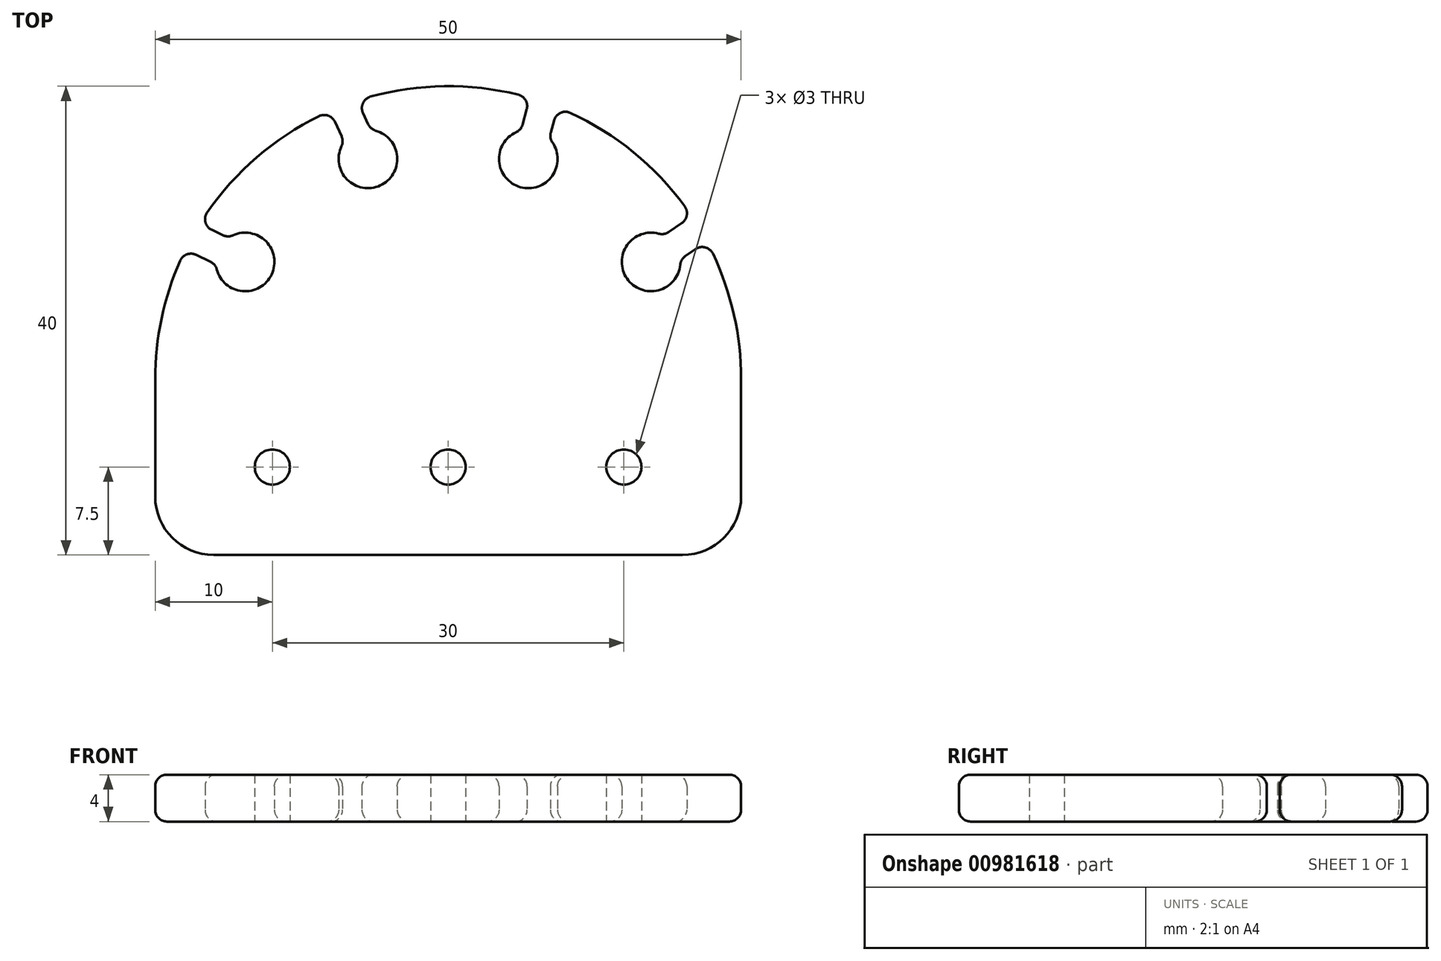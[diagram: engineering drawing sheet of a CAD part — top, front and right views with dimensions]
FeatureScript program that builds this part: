
annotation { "Feature Type Name" : "Feature", "Feature Type Description" : "" }
export const myFeature = defineFeature(function(context is Context, id is Id, definition is map)
    precondition{}
    {
        {
            var Q0;
            Q0=qCreatedBy(makeId("Top.planeOp"),FACE);
            var sketch = newSketch(context, id + "F0", { "sketchPlane" : qUnion([Q0])});
            skCircle(sketch, "E0", {"center": v(-17.32, 25) * mm, "radius": 2.5 * mm});
            skLineSegment(sketch, "E1", {"start": v(-17.32, 25) * mm, "end": v(-21.85, 27.15) * mm, "construction": true});
            skLineSegment(sketch, "E2.0", {"start": v(-14.98, 25.27) * mm, "end": v(-22.2, 28.7) * mm});
            skLineSegment(sketch, "E3.MirrorCS", {"start": v(-16.05, 23.01) * mm, "end": v(-23.28, 26.45) * mm});
            skCircle(sketch, "E4", {"center": v(0, 15) * mm, "radius": 25 * mm});
            skCircle(sketch, "E5.1.0", {"center": v(-6.84, 33.8) * mm, "radius": 2.5 * mm});
            skLineSegment(sketch, "E5.1.1", {"start": v(-7.15, 31.46) * mm, "end": v(-10.47, 38.73) * mm});
            skLineSegment(sketch, "E5.1.2", {"start": v(-4.87, 32.5) * mm, "end": v(-8.2, 39.77) * mm});
            skCircle(sketch, "E5.2.0", {"center": v(6.84, 33.8) * mm, "radius": 2.5 * mm});
            skLineSegment(sketch, "E5.2.1", {"start": v(5.1, 32.2) * mm, "end": v(7.23, 39.91) * mm});
            skLineSegment(sketch, "E5.2.2", {"start": v(7.51, 31.53) * mm, "end": v(9.64, 39.25) * mm});
            skCircle(sketch, "E5.3.0", {"center": v(17.32, 25) * mm, "radius": 2.5 * mm});
            skLineSegment(sketch, "E5.3.1", {"start": v(14.96, 24.9) * mm, "end": v(21.55, 29.43) * mm});
            skLineSegment(sketch, "E5.3.2", {"start": v(16.38, 22.84) * mm, "end": v(22.97, 27.38) * mm});
            skLineSegment(sketch, "E5.anchor1", {"start": v(0, 15) * mm, "end": v(-17.32, 25) * mm, "construction": true});
            skLineSegment(sketch, "E5.anchor2", {"start": v(0, 15) * mm, "end": v(17.32, 25) * mm, "construction": true});
            skLineSegment(sketch, "E6.bottom", {"start": v(-25, 15) * mm, "end": v(25, 15) * mm});
            skLineSegment(sketch, "E6.left", {"start": v(-25, 15) * mm, "end": v(-25, 0) * mm});
            skLineSegment(sketch, "E6.right", {"start": v(25, 15) * mm, "end": v(25, 0) * mm});
            skLineSegment(sketch, "E7", {"start": v(-25, 0) * mm, "end": v(25, 0) * mm});
            skLineSegment(sketch, "E8", {"start": v(-25, 7.5) * mm, "end": v(25, 7.5) * mm, "construction": true});
            skCircle(sketch, "E9", {"center": v(-15, 7.5) * mm, "radius": 1.5 * mm});
            skCircle(sketch, "E10", {"center": v(0, 7.5) * mm, "radius": 1.5 * mm});
            skCircle(sketch, "E11", {"center": v(15, 7.5) * mm, "radius": 1.5 * mm});
            skSolve(sketch);
        }
        {
            var Q0;
            {var subQ20=sQuery(id+"F0.wireOp",EDGE,"E6.bottom");Q0=makeQuery(id+"F0.imprint","IMPRINT",FACE,{"disambiguationData":[TD([[makeQuery(id+"F0.imprint","IMPRINT",EDGE,{"derivedFrom":subQ20}),1.0]])]});}
            var Q1;
            {var subQ4=sQuery(id+"F0.wireOp",EDGE,"E6.bottom");Q1=makeQuery(id+"F0.imprint","IMPRINT",FACE,{"disambiguationData":[TD([[makeQuery(id+"F0.imprint","IMPRINT",EDGE,{"derivedFrom":subQ4}),-1.0]])]});}
            var Q2;
            {var subQ0=sQuery(id+"F0.wireOp",EDGE,"E6.left");Q2=makeQuery(id+"F0.imprint","IMPRINT",FACE,{"disambiguationData":[TD([[makeQuery(id+"F0.imprint","IMPRINT",EDGE,{"derivedFrom":subQ0}),1.0]])]});}
            var Q3;
            {var subQ0=sQuery(id+"F0.wireOp",EDGE,"E6.right");Q3=makeQuery(id+"F0.imprint","IMPRINT",FACE,{"disambiguationData":[TD([[makeQuery(id+"F0.imprint","IMPRINT",EDGE,{"derivedFrom":subQ0}),-1.0]])]});}
            extrude(context, id + "F1", {"entities" : qUnion([Q0, Q1, Q2, Q3]), "depth" : 4 * mm, "offsetDistance" : 25 * mm});
        }
        {
            var Q0;
            Q0=makeQuery(id+"F1.opExtrude","SWEPT_EDGE",EDGE,{"disambiguationData":[OSD([sQuery(id+"F0.wireOp",EDGE,"E6.left"),sQuery(id+"F0.wireOp",EDGE,"E7")])]});
            var Q1;
            Q1=makeQuery(id+"F1.opExtrude","SWEPT_EDGE",EDGE,{"disambiguationData":[OSD([sQuery(id+"F0.wireOp",EDGE,"E6.right"),sQuery(id+"F0.wireOp",EDGE,"E7")])]});
            fillet(context, id + "F2", {"entities" : qUnion([Q0, Q1]), "radius" : 5 * mm, "tangentPropagation" : true, "allowEdgeOverflow" : false});
        }
        {
            var Q0;
            Q0=makeQuery(id+"F1.opExtrude","SWEPT_EDGE",EDGE,{"disambiguationData":[OSD([sQuery(id+"F0.wireOp",EDGE,"E4"),sQuery(id+"F0.wireOp",EDGE,"E5.3.2")])]});
            var Q1;
            Q1=makeQuery(id+"F1.opExtrude","SWEPT_EDGE",EDGE,{"disambiguationData":[OSD([sQuery(id+"F0.wireOp",EDGE,"E4"),sQuery(id+"F0.wireOp",EDGE,"E5.3.1")])]});
            var Q2;
            Q2=makeQuery(id+"F1.opExtrude","SWEPT_EDGE",EDGE,{"disambiguationData":[OSD([sQuery(id+"F0.wireOp",EDGE,"E4"),sQuery(id+"F0.wireOp",EDGE,"E5.2.2")])]});
            var Q3;
            Q3=makeQuery(id+"F1.opExtrude","SWEPT_EDGE",EDGE,{"disambiguationData":[OSD([sQuery(id+"F0.wireOp",EDGE,"E4"),sQuery(id+"F0.wireOp",EDGE,"E5.2.1")])]});
            var Q4;
            Q4=makeQuery(id+"F1.opExtrude","SWEPT_EDGE",EDGE,{"disambiguationData":[OSD([sQuery(id+"F0.wireOp",EDGE,"E4"),sQuery(id+"F0.wireOp",EDGE,"E5.1.2")])]});
            var Q5;
            Q5=makeQuery(id+"F1.opExtrude","SWEPT_EDGE",EDGE,{"disambiguationData":[OSD([sQuery(id+"F0.wireOp",EDGE,"E4"),sQuery(id+"F0.wireOp",EDGE,"E5.1.1")])]});
            var Q6;
            Q6=makeQuery(id+"F1.opExtrude","SWEPT_EDGE",EDGE,{"disambiguationData":[OSD([sQuery(id+"F0.wireOp",EDGE,"E2.0"),sQuery(id+"F0.wireOp",EDGE,"E4")])]});
            var Q7;
            Q7=makeQuery(id+"F1.opExtrude","SWEPT_EDGE",EDGE,{"disambiguationData":[OSD([sQuery(id+"F0.wireOp",EDGE,"E3.MirrorCS"),sQuery(id+"F0.wireOp",EDGE,"E4")])]});
            var Q8;
            Q8=makeQuery(id+"F1.opExtrude","SWEPT_EDGE",EDGE,{"disambiguationData":[OSD([sQuery(id+"F0.wireOp",EDGE,"E0"),sQuery(id+"F0.wireOp",EDGE,"E2.0")])]});
            var Q9;
            Q9=makeQuery(id+"F1.opExtrude","SWEPT_EDGE",EDGE,{"disambiguationData":[OSD([sQuery(id+"F0.wireOp",EDGE,"E0"),sQuery(id+"F0.wireOp",EDGE,"E3.MirrorCS")])]});
            var Q10;
            Q10=makeQuery(id+"F1.opExtrude","SWEPT_EDGE",EDGE,{"disambiguationData":[OSD([sQuery(id+"F0.wireOp",EDGE,"E5.1.0"),sQuery(id+"F0.wireOp",EDGE,"E5.1.1")])]});
            var Q11;
            Q11=makeQuery(id+"F1.opExtrude","SWEPT_EDGE",EDGE,{"disambiguationData":[OSD([sQuery(id+"F0.wireOp",EDGE,"E5.1.0"),sQuery(id+"F0.wireOp",EDGE,"E5.1.2")])]});
            var Q12;
            Q12=makeQuery(id+"F1.opExtrude","SWEPT_EDGE",EDGE,{"disambiguationData":[OSD([sQuery(id+"F0.wireOp",EDGE,"E5.2.0"),sQuery(id+"F0.wireOp",EDGE,"E5.2.2")])]});
            var Q13;
            Q13=makeQuery(id+"F1.opExtrude","SWEPT_EDGE",EDGE,{"disambiguationData":[OSD([sQuery(id+"F0.wireOp",EDGE,"E5.2.0"),sQuery(id+"F0.wireOp",EDGE,"E5.2.1")])]});
            var Q14;
            Q14=makeQuery(id+"F1.opExtrude","SWEPT_EDGE",EDGE,{"disambiguationData":[OSD([sQuery(id+"F0.wireOp",EDGE,"E5.3.0"),sQuery(id+"F0.wireOp",EDGE,"E5.3.1")])]});
            var Q15;
            Q15=makeQuery(id+"F1.opExtrude","SWEPT_EDGE",EDGE,{"disambiguationData":[OSD([sQuery(id+"F0.wireOp",EDGE,"E5.3.0"),sQuery(id+"F0.wireOp",EDGE,"E5.3.2")])]});
            fillet(context, id + "F3", {"entities" : qUnion([Q0, Q1, Q2, Q3, Q4, Q5, Q6, Q7, Q8, Q9, Q10, Q11, Q12, Q13, Q14, Q15]), "radius" : 1 * mm, "tangentPropagation" : true, "allowEdgeOverflow" : false});
        }
        {
            var Q0;
            {var subQ0=sQuery(id+"F0.wireOp",EDGE,"E4");Q0=makeQuery(id+"F1.opExtrude","CAP_EDGE",EDGE,{"disambiguationData":[OSD([subQ0]),TDD([makeQuery(id+"F0.imprint","IMPRINT",EDGE,{"disambiguationData":[TD([[makeQuery(id+"F0.imprint","INTERSECT",VERTEX,{"derivedFrom":[subQ0,sQuery(id+"F0.wireOp",EDGE,"E5.3.1")]}),-1.0]])],"derivedFrom":subQ0})])],"isStart":false});}
            var Q1;
            {var subQ0=sQuery(id+"F0.wireOp",EDGE,"E4");Q1=makeQuery(id+"F1.opExtrude","CAP_EDGE",EDGE,{"disambiguationData":[OSD([subQ0]),TDD([makeQuery(id+"F0.imprint","IMPRINT",EDGE,{"disambiguationData":[TD([[makeQuery(id+"F0.imprint","INTERSECT",VERTEX,{"derivedFrom":[subQ0,sQuery(id+"F0.wireOp",EDGE,"E5.3.1")]}),-1.0]])],"derivedFrom":subQ0})])],"isStart":true});}
            fillet(context, id + "F4", {"entities" : qUnion([Q0, Q1]), "radius" : 1 * mm, "tangentPropagation" : true, "allowEdgeOverflow" : false});
        }
    });
